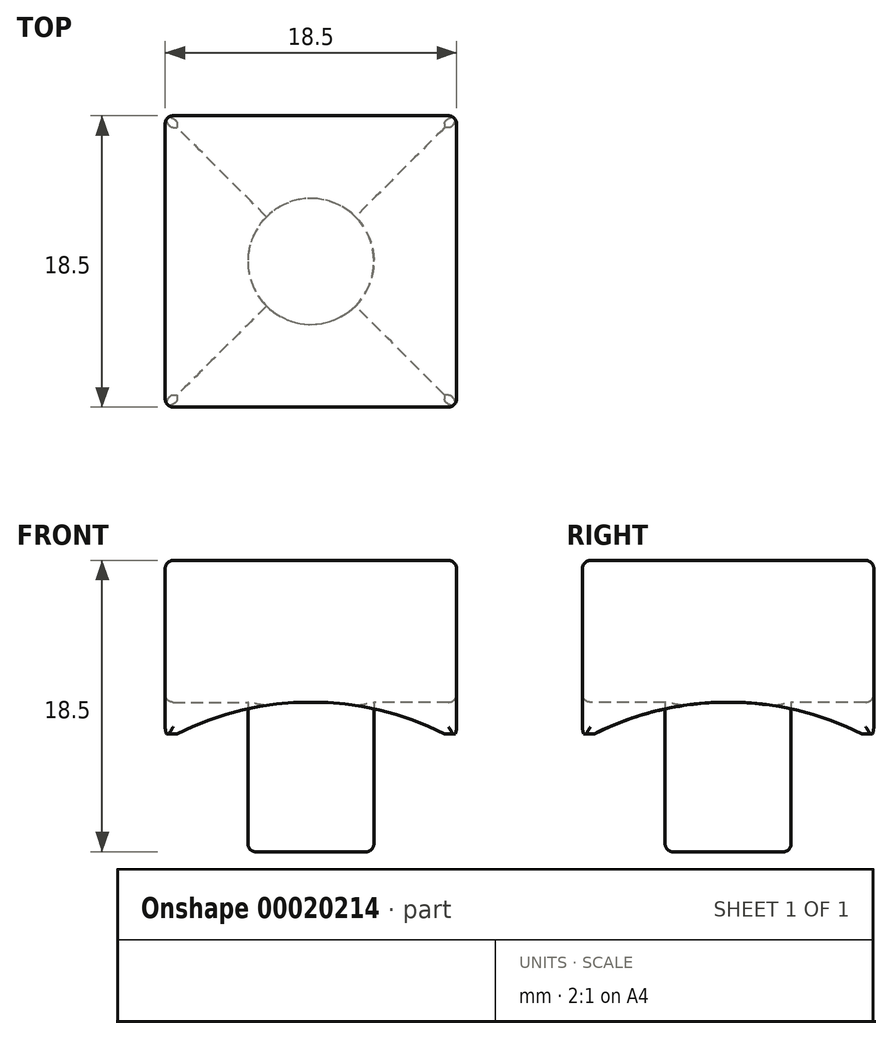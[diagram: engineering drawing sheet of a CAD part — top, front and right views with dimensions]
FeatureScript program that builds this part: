
annotation { "Feature Type Name" : "Feature", "Feature Type Description" : "" }
export const myFeature = defineFeature(function(context is Context, id is Id, definition is map)
    precondition{}
    {
        {
            var Q0;
            Q0=qCreatedBy(makeId("Front.planeOp"),FACE);
            var sketch = newSketch(context, id + "F0", { "sketchPlane" : qUnion([Q0])});
            skLineSegment(sketch, "E0.rect.bottom", {"start": v(9.25, 5.5) * mm, "end": v(-9.25, 5.5) * mm});
            skLineSegment(sketch, "E0.rect.top", {"start": v(9.25, -5.5) * mm, "end": v(-9.25, -5.5) * mm});
            skLineSegment(sketch, "E0.rect.left", {"start": v(9.25, 5.5) * mm, "end": v(9.25, -5.5) * mm});
            skLineSegment(sketch, "E0.rect.right", {"start": v(-9.25, 5.5) * mm, "end": v(-9.25, -5.5) * mm});
            skPoint(sketch, "E0.rect.middle", {"position": v(0, 0) * mm});
            skSolve(sketch);
        }
        {
            var Q0;
            Q0=makeQuery(id+"F0.imprint","IMPRINT",FACE,{"disambiguationData":[TD([[makeQuery(id+"F0.imprint","IMPRINT",EDGE,{"derivedFrom":sQuery(id+"F0.wireOp",EDGE,"E0.rect.bottom")}),1.0]])]});
            extrude(context, id + "F1", {"entities" : qUnion([Q0]), "oppositeDirection" : true, "depth" : 9.25 * mm});
        }
        {
            var Q0;
            Q0=qSketchRegion(id+"F0",true);
            extrude(context, id + "F2", {"entities" : qUnion([Q0]), "operationType" : NewBodyOperationType.ADD, "depth" : 9.25 * mm});
        }
        {
            var Q0;
            Q0=qCreatedBy(makeId("Front.planeOp"),FACE);
            var sketch = newSketch(context, id + "F3", { "sketchPlane" : qUnion([Q0])});
            skPoint(sketch, "E1", {"position": v(0, -3.5) * mm});
            skCircle(sketch, "E2", {"center": v(0, -22.5) * mm, "radius": 19 * mm});
            skSolve(sketch);
        }
        {
            var Q0;
            Q0=qCreatedBy(makeId("Right.planeOp"),FACE);
            var sketch = newSketch(context, id + "F4", { "sketchPlane" : qUnion([Q0])});
            skPoint(sketch, "E3", {"position": v(0, -3.5) * mm});
            skCircle(sketch, "E4", {"center": v(0, -22.5) * mm, "radius": 19 * mm});
            skSolve(sketch);
        }
        {
            var Q0;
            Q0=qSketchRegion(id+"F9",true);
            var Q1;
            Q1=qSketchRegion(id+"F3",true);
            extrude(context, id + "F5", {"entities" : qUnion([Q0, Q1]), "operationType" : NewBodyOperationType.REMOVE, "oppositeDirection" : true, "depth" : 25.4 * mm});
        }
        {
            var Q0;
            Q0=qSketchRegion(id+"F3",true);
            extrude(context, id + "F6", {"entities" : qUnion([Q0]), "operationType" : NewBodyOperationType.REMOVE, "depth" : 25.4 * mm});
        }
        {
            var Q0;
            Q0=qSketchRegion(id+"F4",true);
            extrude(context, id + "F7", {"entities" : qUnion([Q0]), "operationType" : NewBodyOperationType.REMOVE, "oppositeDirection" : true, "depth" : 25.4 * mm});
        }
        {
            var Q0;
            Q0=qSketchRegion(id+"F4",true);
            extrude(context, id + "F8", {"entities" : qUnion([Q0]), "operationType" : NewBodyOperationType.REMOVE, "depth" : 25.4 * mm});
        }
        {
            var Q0;
            {var subQ0=sQuery(id+"F0.wireOp",EDGE,"E0.rect.top");Q0=makeQuery(id+"F2.boolean.opBoolean","MERGE",FACE,{"derivedFrom":[makeQuery(id+"F1.opExtrude","SWEPT_FACE",FACE,{"disambiguationData":[OSD([subQ0])]}),makeQuery(id+"F2.opExtrude","SWEPT_FACE",FACE,{"disambiguationData":[OSD([subQ0])]})]});}
            var sketch = newSketch(context, id + "F9", { "sketchPlane" : qUnion([Q0])});
            skCircle(sketch, "E5", {"center": v(0, 0) * mm, "radius": 4 * mm});
            skSolve(sketch);
        }
        {
            var Q0;
            Q0=qSketchRegion(id+"F9",true);
            extrude(context, id + "F10", {"entities" : qUnion([Q0]), "operationType" : NewBodyOperationType.ADD, "oppositeDirection" : true, "depth" : 3.46 * mm});
        }
        {
            var Q0;
            Q0=makeQuery(id+"F10.opExtrude","CAP_FACE",FACE,{"disambiguationData":[OSD([sQuery(id+"F9.wireOp",EDGE,"E5")])],"isStart":true});
            extrude(context, id + "F11", {"entities" : qUnion([Q0]), "operationType" : NewBodyOperationType.ADD, "depth" : 7.5 * mm});
        }
        {
            var Q0;
            Q0=makeQuery(id+"F2.opExtrude","CAP_EDGE",EDGE,{"disambiguationData":[OSD([sQuery(id+"F0.wireOp",EDGE,"E0.rect.left")])],"isStart":false});
            var Q1;
            Q1=makeQuery(id+"F2.opExtrude","CAP_EDGE",EDGE,{"disambiguationData":[OSD([sQuery(id+"F0.wireOp",EDGE,"E0.rect.bottom")])],"isStart":false});
            var Q2;
            {var subQ0=sQuery(id+"F0.wireOp",EDGE,"E0.rect.bottom");var subQ1=sQuery(id+"F0.wireOp",EDGE,"E0.rect.left");Q2=makeQuery(id+"F2.boolean.opBoolean","MERGE",EDGE,{"derivedFrom":[makeQuery(id+"F1.opExtrude","SWEPT_EDGE",EDGE,{"disambiguationData":[OSD([subQ0,subQ1])]}),makeQuery(id+"F2.opExtrude","SWEPT_EDGE",EDGE,{"disambiguationData":[OSD([subQ0,subQ1])]})]});}
            var Q3;
            Q3=makeQuery(id+"F1.opExtrude","CAP_EDGE",EDGE,{"disambiguationData":[OSD([sQuery(id+"F0.wireOp",EDGE,"E0.rect.bottom")])],"isStart":false});
            var Q4;
            {var subQ0=sQuery(id+"F0.wireOp",EDGE,"E0.rect.bottom");var subQ1=sQuery(id+"F0.wireOp",EDGE,"E0.rect.right");Q4=makeQuery(id+"F2.boolean.opBoolean","MERGE",EDGE,{"derivedFrom":[makeQuery(id+"F1.opExtrude","SWEPT_EDGE",EDGE,{"disambiguationData":[OSD([subQ0,subQ1])]}),makeQuery(id+"F2.opExtrude","SWEPT_EDGE",EDGE,{"disambiguationData":[OSD([subQ0,subQ1])]})]});}
            var Q5;
            Q5=makeQuery(id+"F2.opExtrude","CAP_EDGE",EDGE,{"disambiguationData":[OSD([sQuery(id+"F0.wireOp",EDGE,"E0.rect.right")])],"isStart":false});
            var Q6;
            Q6=makeQuery(id+"F1.opExtrude","CAP_EDGE",EDGE,{"disambiguationData":[OSD([sQuery(id+"F0.wireOp",EDGE,"E0.rect.left")])],"isStart":false});
            var Q7;
            Q7=makeQuery(id+"F1.opExtrude","CAP_EDGE",EDGE,{"disambiguationData":[OSD([sQuery(id+"F0.wireOp",EDGE,"E0.rect.right")])],"isStart":false});
            var Q8;
            Q8=makeQuery(id+"F11.opExtrude","CAP_EDGE",EDGE,{"disambiguationData":[OSD([sQuery(id+"F9.wireOp",EDGE,"E5")])],"isStart":false});
            var Q9;
            Q9=makeQuery(id+"F6.boolean.opBoolean","INTERSECT",EDGE,{"derivedFrom":[makeQuery(id+"F2.opExtrude","CAP_FACE",FACE,{"disambiguationData":[OSD([sQuery(id+"F0.wireOp",EDGE,"E0.rect.bottom"),sQuery(id+"F0.wireOp",EDGE,"E0.rect.top"),sQuery(id+"F0.wireOp",EDGE,"E0.rect.left"),sQuery(id+"F0.wireOp",EDGE,"E0.rect.right")])],"isStart":false}),makeQuery(id+"F6.opExtrude","SWEPT_FACE",FACE,{"disambiguationData":[OSD([sQuery(id+"F3.wireOp",EDGE,"E2")])]})]});
            var Q10;
            {var subQ0=sQuery(id+"F0.wireOp",EDGE,"E0.rect.right");Q10=makeQuery(id+"F7.boolean.opBoolean","INTERSECT",EDGE,{"derivedFrom":[makeQuery(id+"F2.boolean.opBoolean","MERGE",FACE,{"derivedFrom":[makeQuery(id+"F1.opExtrude","SWEPT_FACE",FACE,{"disambiguationData":[OSD([subQ0])]}),makeQuery(id+"F2.opExtrude","SWEPT_FACE",FACE,{"disambiguationData":[OSD([subQ0])]})]}),makeQuery(id+"F7.opExtrude","SWEPT_FACE",FACE,{"disambiguationData":[OSD([sQuery(id+"F4.wireOp",EDGE,"E4")])]})]});}
            var Q11;
            {var subQ0=sQuery(id+"F0.wireOp",EDGE,"E0.rect.left");Q11=makeQuery(id+"F8.boolean.opBoolean","INTERSECT",EDGE,{"derivedFrom":[makeQuery(id+"F2.boolean.opBoolean","MERGE",FACE,{"derivedFrom":[makeQuery(id+"F1.opExtrude","SWEPT_FACE",FACE,{"disambiguationData":[OSD([subQ0])]}),makeQuery(id+"F2.opExtrude","SWEPT_FACE",FACE,{"disambiguationData":[OSD([subQ0])]})]}),makeQuery(id+"F8.opExtrude","SWEPT_FACE",FACE,{"disambiguationData":[OSD([sQuery(id+"F4.wireOp",EDGE,"E4")])]})]});}
            var Q12;
            Q12=makeQuery(id+"F5.boolean.opBoolean","INTERSECT",EDGE,{"derivedFrom":[makeQuery(id+"F1.opExtrude","CAP_FACE",FACE,{"disambiguationData":[OSD([sQuery(id+"F0.wireOp",EDGE,"E0.rect.bottom"),sQuery(id+"F0.wireOp",EDGE,"E0.rect.top"),sQuery(id+"F0.wireOp",EDGE,"E0.rect.left"),sQuery(id+"F0.wireOp",EDGE,"E0.rect.right")])],"isStart":false}),makeQuery(id+"F5.opExtrude","SWEPT_FACE",FACE,{"disambiguationData":[OSD([sQuery(id+"F3.wireOp",EDGE,"E2")])]})]});
            fillet(context, id + "F12", {"entities" : qUnion([Q0, Q1, Q2, Q3, Q4, Q5, Q6, Q7, Q8, Q9, Q10, Q11, Q12]), "radius" : .5 * mm, "tangentPropagation" : true, "allowEdgeOverflow" : false});
        }
    });
